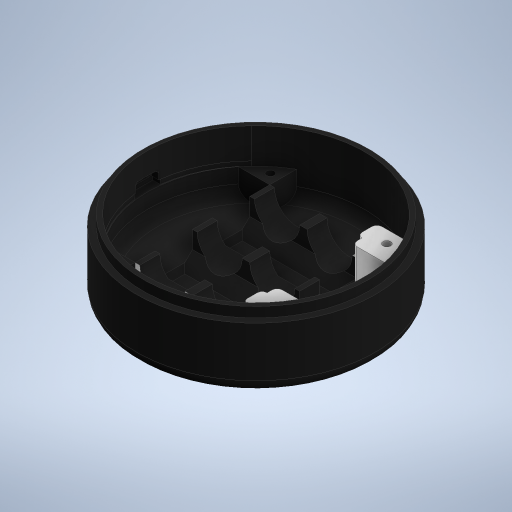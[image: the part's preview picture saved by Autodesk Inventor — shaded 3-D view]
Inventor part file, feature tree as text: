
AUTODESK INVENTOR PART (.ipt)
format: ipt  version: 2024 (Build 280153000, 153)  size: 670,720 bytes
history: native  units: mm
features: extrude x20, sketch x19, projected_geometry x14, chamfer x4, fillet x3, other x1
ambient origin geometry x8: Origin, YZ Plane, XZ Plane, XY Plane, X Axis, Y Axis, Z Axis, Center Point
bodies: Solide1 (feature_tree)
feature tree (61):
  sketch  "Esquisse1"
  extrude  "Extrusion1"  Depth=90.62mm
  extrude  "Extrusion4"  Depth=2.58mm
  fillet  "Congé2"  Radius=20.0mm
  sketch  "Esquisse6"
  sketch  "Esquisse7"
  extrude  "Extrusion5"  Depth=18.0mm
  extrude  "Extrusion6"  Depth=5.0mm TaperAngle=0.0deg
  other  "Plan de construction1"
  extrude  "Extrusion7"  Depth=5.0mm
  extrude  "Extrusion8"  Depth=90.31mm
  sketch  "Esquisse10"
  extrude  "Extrusion9"  Depth=87.0mm
  extrude  "Extrusion10"  Depth=5.0mm TaperAngle=0.0deg
  extrude  "Extrusion11"  Depth=4.0mm TaperAngle=0.0deg
  extrude  "Extrusion12"  Depth=43.0mm
  extrude  "Extrusion13"  Depth=8.0mm
  extrude  "Extrusion14"  Depth=43.0mm
  extrude  "Extrusion15"  Depth=43.0mm
  extrude  "Extrusion16"  Depth=15.0mm
  extrude  "Extrusion17"  Depth=10.0mm TaperAngle=0.0deg
  sketch  "Esquisse19"
  extrude  "Extrusion18"  Depth=18.1mm
  extrude  "Extrusion19"  Depth=18.1mm
  fillet  "Congé5"  Radius=21.1mm
  chamfer  "Chanfrein2"  Distance=10.95mm
  chamfer  "Chanfrein3"  Distance=10.0mm
  extrude  "Extrusion20"  Depth=15.3mm
  chamfer  "Chanfrein4"  Distance=21.3mm
  extrude  "Extrusion21"  Depth=12.5mm
  chamfer  "Chanfrein5"  Distance=20.0mm
  extrude  "Extrusion22"  Depth=5.0mm TaperAngle=0.0deg
  fillet  "Congé6"  Radius=10.0mm
  sketch  "Esquisse23"
  sketch  "Esquisse4"
  projected_geometry  "Boucle projetée3"
  projected_geometry  "Boucle projetée4"
  sketch  "Esquisse8"
  sketch  "Esquisse9"
  projected_geometry  "Boucle projetée5"
  sketch  "Esquisse11"
  projected_geometry  "Boucle projetée6"
  sketch  "Esquisse12"
  projected_geometry  "Boucle projetée7"
  sketch  "Esquisse13"
  projected_geometry  "Boucle projetée8"
  sketch  "Esquisse14"
  projected_geometry  "Boucle projetée9"
  sketch  "Esquisse15"
  sketch  "Esquisse16"
  projected_geometry  "Boucle projetée10"
  projected_geometry  "Boucle projetée11"
  sketch  "Esquisse18"
  projected_geometry  "Boucle projetée13"
  projected_geometry  "Boucle projetée14"
  sketch  "Esquisse20"
  sketch  "Esquisse21"
  projected_geometry  "Boucle projetée15"
  sketch  "Esquisse22"
  projected_geometry  "Boucle projetée16"
  projected_geometry  "Boucle projetée17"
